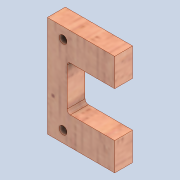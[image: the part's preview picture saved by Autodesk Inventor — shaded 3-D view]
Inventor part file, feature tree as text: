
AUTODESK INVENTOR PART (.ipt)
format: ipt  version: 2020 (Build 240168000, 168)  size: 220,672 bytes
history: native  units: mm
features: other x4, extrude x3, sketch x3, fillet x1, reference x1
ambient origin geometry x8: Origin, YZ Plane, XZ Plane, XY Plane, X Axis, Y Axis, Z Axis, Center Point
bodies: Solid1 (feature_tree)
feature tree (12):
  extrude  "Extrusion1"  Depth=45.0mm
  extrude  "Extrusion3"  TaperAngle=0.0deg  [1 undecoded]
  extrude  "Extrusion4"  Depth=10.0mm TaperAngle=0.0deg
  fillet  "Fillet1"  [1 undecoded]
  sketch  "Sketch1"  dims[d0=30.0mm d1=45.0mm]
  sketch  "Sketch3"  dims[d2=8.0mm d3=0.0mm d8=0.0mm]
  reference  "Reference1"
  sketch  "Sketch4"  dims[d9=20.0mm d10=10.0mm d11=0.0mm d15=0.0mm d16=0.0mm d17=3.5mm d18=3.5mm d19=5.0mm d20=7.0mm d21=5.0mm d22=35.0mm d23=1.5mm]
  parser-record x1  (decoder bookkeeping rows leaked as tree rows — omitted from the tree; the rows remain in map.json)
  other  "0005-00-00 Ansamblu_General.iam"
  other  "Plunger Assembly_Défaut:1"
  other  "plunger_Défaut_4"
note: 2 required parameter values undecoded (feature->parameter linkage not recoverable at this tier; creation-order binding heuristic only, values carry confidence <= 0.55)
note: 1 file-system path scrubbed to <path> (originals preserved in map.json)
